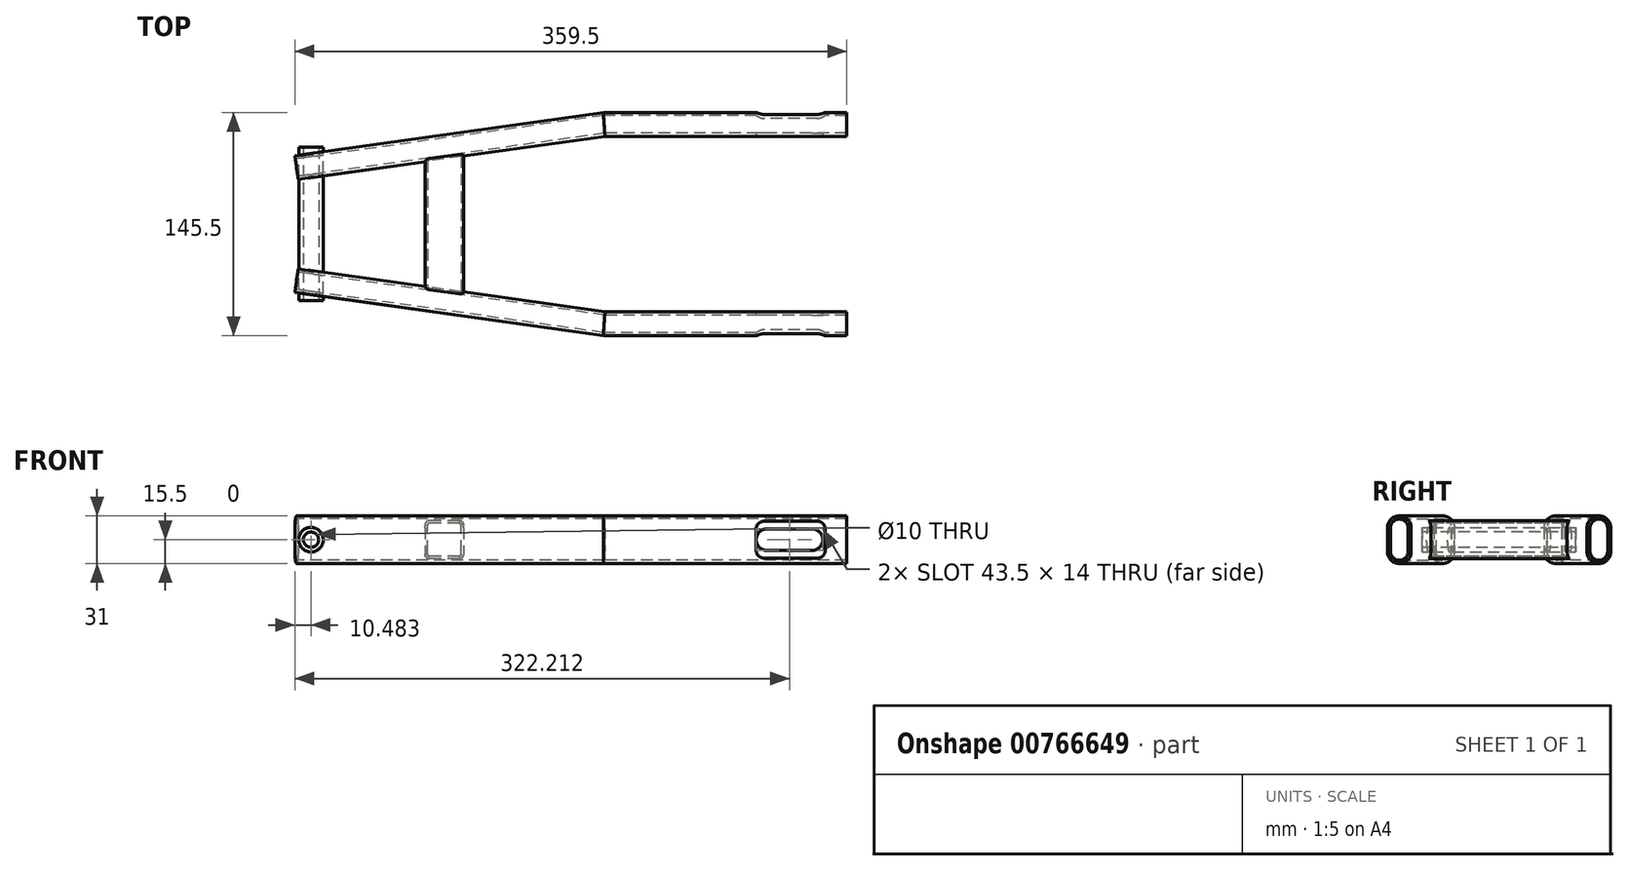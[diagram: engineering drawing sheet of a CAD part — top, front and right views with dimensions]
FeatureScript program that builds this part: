
annotation { "Feature Type Name" : "Feature", "Feature Type Description" : "" }
export const myFeature = defineFeature(function(context is Context, id is Id, definition is map)
    precondition{}
    {
        {
            var Q0;
            Q0=qCreatedBy(makeId("Top.planeOp"),FACE);
            var sketch = newSketch(context, id + "F0", { "sketchPlane" : qUnion([Q0])});
            skLineSegment(sketch, "E0", {"start": v(150.18, 0) * mm, "end": v(-148.55, 0) * mm, "construction": true});
            skLineSegment(sketch, "E1", {"start": v(150.18, 65) * mm, "end": v(-150.97, 65) * mm, "construction": true});
            skLineSegment(sketch, "E2", {"start": v(150.18, 65) * mm, "end": v(-7.85, 65) * mm});
            skLineSegment(sketch, "E3", {"start": v(-7.85, 65) * mm, "end": v(-208.24, 36.84) * mm});
            skSolve(sketch);
        }
        {
            var Q0;
            Q0=sQuery(id+"F0.wireOp",VERTEX,"E0.start");
            var Q1;
            Q1=qCreatedBy(makeId("Right.planeOp"),FACE);
            cPlane(context, id + "F1", {"entities" : qUnion([Q0, Q1]), "cplaneType" : CPlaneType.PLANE_POINT, "offset" : 25 * mm, "width" : 150 * mm, "height" : 150 * mm});
        }
        {
            var Q0;
            Q0=qCreatedBy(id+"F1.planeOp",FACE);
            var sketch = newSketch(context, id + "F2", { "sketchPlane" : qUnion([Q0])});
            skPoint(sketch, "E4.middle", {"position": v(47.26, 0) * mm});
            skLineSegment(sketch, "E5.left", {"start": v(57.25, 7.75) * mm, "end": v(57.25, -7.75) * mm});
            skLineSegment(sketch, "E5.right", {"start": v(72.75, 7.75) * mm, "end": v(72.75, -7.75) * mm});
            skPoint(sketch, "E5.middle", {"position": v(65, 0) * mm});
            skArc(sketch, "E6", {"start": v(57.25, 7.75) * mm, "mid": v(65, 15.5) * mm, "end": v(72.75, 7.75) * mm});
            skArc(sketch, "E7", {"start": v(57.25, -7.75) * mm, "mid": v(65, -15.5) * mm, "end": v(72.75, -7.75) * mm});
            skLineSegment(sketch, "E8.0", {"start": v(59.25, 7.75) * mm, "end": v(59.25, -7.75) * mm});
            skLineSegment(sketch, "E9.MirrorCS", {"start": v(70.75, 7.75) * mm, "end": v(70.75, -7.75) * mm});
            skPoint(sketch, "E10.start.orphan", {"position": v(65, 15.5) * mm});
            skPoint(sketch, "E11.trimOffspring.end.orphan", {"position": v(65, -15.5) * mm});
            skArc(sketch, "E12", {"start": v(59.25, 7.75) * mm, "mid": v(65, 13.5) * mm, "end": v(70.75, 7.75) * mm});
            skArc(sketch, "E13", {"start": v(59.25, -7.75) * mm, "mid": v(65, -13.5) * mm, "end": v(70.75, -7.75) * mm});
            skSolve(sketch);
        }
        {
            var Q0;
            Q0 = qSketchRegion(id + "F2", true);
            var Q1;
            Q1 = qConstructionFilter(qBodyType(qCreatedBy(id + "F0" ,EDGE), BodyType.WIRE), ConstructionObject.NO);
            sweep(context, id + "F3", {"profiles" : qUnion([Q0]), "path" : qUnion([Q1])});
        }
        {
            var Q0;
            Q0=makeQuery(id+"F3.opSweep","SWEPT_FACE",FACE,{"disambiguationData":[OSD([sQuery(id+"F0.wireOp",EDGE,"E2"),sQuery(id+"F2.wireOp",EDGE,"E5.left")])]});
            var sketch = newSketch(context, id + "F4", { "sketchPlane" : qUnion([Q0])});
            skLineSegment(sketch, "E14.bottom", {"start": v(127.64, -7) * mm, "end": v(98.14, -7) * mm});
            skLineSegment(sketch, "E14.top", {"start": v(127.64, 7) * mm, "end": v(98.14, 7) * mm});
            skPoint(sketch, "E14.middle", {"position": v(112.9, 0) * mm});
            skArc(sketch, "E15", {"start": v(127.64, 7) * mm, "mid": v(134.64, 0) * mm, "end": v(127.64, -7) * mm});
            skArc(sketch, "E16", {"start": v(98.14, 7) * mm, "mid": v(91.14, 0) * mm, "end": v(98.14, -7) * mm});
            skSolve(sketch);
        }
        {
            var Q0;
            Q0 = qSketchRegion(id + "F4", true);
            extrude(context, id + "F5", {"entities" : qUnion([Q0]), "operationType" : NewBodyOperationType.REMOVE, "endBound" : BoundingType.UP_TO_NEXT, "oppositeDirection" : true, "depth" : 25 * mm, "offsetDistance" : 25 * mm});
        }
        {
            var Q0;
            Q0=makeQuery(id+"F3.opSweep","SWEPT_BODY",BODY,{"disambiguationData":[OSD([sQuery(id+"F0.wireOp",EDGE,"E3"),sQuery(id+"F2.wireOp",EDGE,"E5.left"),sQuery(id+"F2.wireOp",EDGE,"E5.right"),sQuery(id+"F2.wireOp",EDGE,"E6"),sQuery(id+"F2.wireOp",EDGE,"E7"),sQuery(id+"F2.wireOp",EDGE,"E8.0"),sQuery(id+"F2.wireOp",EDGE,"E9.MirrorCS"),sQuery(id+"F2.wireOp",EDGE,"E12"),sQuery(id+"F2.wireOp",EDGE,"E13")])]});
            var Q1;
            Q1=qCreatedBy(makeId("Front.planeOp"),FACE);
            mirror(context, id + "F6", {"entities" : qUnion([Q0]), "mirrorPlane" : qUnion([Q1])});
        }
        {
            var Q0;
            Q0=makeQuery(id+"F6.opPattern","COPY",FACE,{"derivedFrom":makeQuery(id+"F3.opSweep","SWEPT_FACE",FACE,{"disambiguationData":[OSD([sQuery(id+"F0.wireOp",EDGE,"E2"),sQuery(id+"F2.wireOp",EDGE,"E5.right")])]}),"instanceName":"1"});
            var sketch = newSketch(context, id + "F7", { "sketchPlane" : qUnion([Q0])});
            skLineSegment(sketch, "E17.bottom", {"start": v(96.18, 12) * mm, "end": v(131.18, 12) * mm});
            skLineSegment(sketch, "E17.top", {"start": v(96.18, -12) * mm, "end": v(131.18, -12) * mm});
            skLineSegment(sketch, "E17.left", {"start": v(91.18, 7) * mm, "end": v(91.18, -7) * mm});
            skLineSegment(sketch, "E17.right", {"start": v(136.18, 7) * mm, "end": v(136.18, -7) * mm});
            skPoint(sketch, "E17.middle", {"position": v(113.68, 0) * mm});
            skPoint(sketch, "E18.visualSharp", {"position": v(91.18, 12) * mm});
            skArc(sketch, "E18.filletArc", {"start": v(96.18, 12) * mm, "mid": v(92.65, 10.54) * mm, "end": v(91.18, 7) * mm});
            skPoint(sketch, "E19.visualSharp", {"position": v(91.18, -12) * mm});
            skArc(sketch, "E19.filletArc", {"start": v(91.18, -7) * mm, "mid": v(92.65, -10.54) * mm, "end": v(96.18, -12) * mm});
            skPoint(sketch, "E20.visualSharp", {"position": v(136.18, 12) * mm});
            skArc(sketch, "E20.filletArc", {"start": v(136.18, 7) * mm, "mid": v(134.72, 10.54) * mm, "end": v(131.18, 12) * mm});
            skPoint(sketch, "E21.visualSharp", {"position": v(136.18, -12) * mm});
            skArc(sketch, "E21.filletArc", {"start": v(131.18, -12) * mm, "mid": v(134.72, -10.54) * mm, "end": v(136.18, -7) * mm});
            skSolve(sketch);
        }
        {
            var Q0;
            Q0 = qSketchRegion(id + "F7", true);
            extrude(context, id + "F8", {"entities" : qUnion([Q0]), "operationType" : NewBodyOperationType.REMOVE, "endBound" : BoundingType.UP_TO_NEXT, "oppositeDirection" : true, "depth" : 25 * mm, "offsetDistance" : 25 * mm});
        }
        {
            var Q0;
            Q0=makeQuery(id+"F3.opSweep","SWEPT_FACE",FACE,{"disambiguationData":[OSD([sQuery(id+"F0.wireOp",EDGE,"E2"),sQuery(id+"F2.wireOp",EDGE,"E5.right")])]});
            var sketch = newSketch(context, id + "F9", { "sketchPlane" : qUnion([Q0])});
            skLineSegment(sketch, "E22.bottom", {"start": v(-131.18, 12) * mm, "end": v(-96.18, 12) * mm});
            skLineSegment(sketch, "E22.top", {"start": v(-131.18, -12) * mm, "end": v(-96.18, -12) * mm});
            skLineSegment(sketch, "E22.left", {"start": v(-136.18, 7) * mm, "end": v(-136.18, -7) * mm});
            skLineSegment(sketch, "E22.right", {"start": v(-91.18, 7) * mm, "end": v(-91.18, -7) * mm});
            skPoint(sketch, "E22.middle", {"position": v(-113.68, 0) * mm});
            skPoint(sketch, "E23.visualSharp", {"position": v(-136.18, 12) * mm});
            skArc(sketch, "E23.filletArc", {"start": v(-131.18, 12) * mm, "mid": v(-134.72, 10.54) * mm, "end": v(-136.18, 7) * mm});
            skPoint(sketch, "E24.visualSharp", {"position": v(-136.18, -12) * mm});
            skArc(sketch, "E24.filletArc", {"start": v(-136.18, -7) * mm, "mid": v(-134.72, -10.54) * mm, "end": v(-131.18, -12) * mm});
            skPoint(sketch, "E25.visualSharp", {"position": v(-91.18, 12) * mm});
            skArc(sketch, "E25.filletArc", {"start": v(-91.18, 7) * mm, "mid": v(-92.65, 10.54) * mm, "end": v(-96.18, 12) * mm});
            skPoint(sketch, "E26.visualSharp", {"position": v(-91.18, -12) * mm});
            skArc(sketch, "E26.filletArc", {"start": v(-96.18, -12) * mm, "mid": v(-92.65, -10.54) * mm, "end": v(-91.18, -7) * mm});
            skSolve(sketch);
        }
        {
            var Q0;
            Q0 = qSketchRegion(id + "F9", true);
            extrude(context, id + "F10", {"entities" : qUnion([Q0]), "operationType" : NewBodyOperationType.REMOVE, "endBound" : BoundingType.UP_TO_NEXT, "oppositeDirection" : true, "depth" : 25 * mm, "offsetDistance" : 25 * mm});
        }
        {
            var Q0;
            Q0=qCreatedBy(makeId("Front.planeOp"),FACE);
            var sketch = newSketch(context, id + "F11", { "sketchPlane" : qUnion([Q0])});
            skCircle(sketch, "E27", {"center": v(-198.84, 0) * mm, "radius": 8 * mm});
            skSolve(sketch);
        }
        {
            var Q0;
            Q0 = qSketchRegion(id + "F11", true);
            extrude(context, id + "F12", {"entities" : qUnion([Q0]), "operationType" : NewBodyOperationType.ADD, "endBound" : BoundingType.SYMMETRIC, "depth" : 100 * mm, "offsetDistance" : 25 * mm});
        }
        {
            var Q0;
            Q0=makeQuery(id+"F12.opExtrude","CAP_FACE",FACE,{"disambiguationData":[OSD([sQuery(id+"F11.wireOp",EDGE,"E27")])],"isStart":false});
            var sketch = newSketch(context, id + "F13", { "sketchPlane" : qUnion([Q0])});
            skCircle(sketch, "E28", {"center": v(-198.84, 0) * mm, "radius": 5 * mm});
            skSolve(sketch);
        }
        {
            var Q0;
            Q0 = qSketchRegion(id + "F13", true);
            extrude(context, id + "F14", {"entities" : qUnion([Q0]), "operationType" : NewBodyOperationType.REMOVE, "oppositeDirection" : true, "depth" : 100 * mm, "offsetDistance" : 25 * mm});
        }
        {
            var Q0;
            Q0=qCreatedBy(makeId("Front.planeOp"),FACE);
            var sketch = newSketch(context, id + "F15", { "sketchPlane" : qUnion([Q0])});
            skLineSegment(sketch, "E29.bottom", {"start": v(-102.5, -12.5) * mm, "end": v(-121.5, -12.5) * mm});
            skLineSegment(sketch, "E29.top", {"start": v(-102.5, 12.5) * mm, "end": v(-121.5, 12.5) * mm});
            skLineSegment(sketch, "E29.left", {"start": v(-99.5, -9.5) * mm, "end": v(-99.5, 9.5) * mm});
            skLineSegment(sketch, "E29.right", {"start": v(-124.5, -9.5) * mm, "end": v(-124.5, 9.5) * mm});
            skPoint(sketch, "E29.middle", {"position": v(-112, 0) * mm});
            skLineSegment(sketch, "E30.bottom", {"start": v(-121.5, -10.9) * mm, "end": v(-102.5, -10.9) * mm});
            skLineSegment(sketch, "E30.top", {"start": v(-121.5, 10.9) * mm, "end": v(-102.5, 10.9) * mm});
            skLineSegment(sketch, "E30.left", {"start": v(-122.9, -9.5) * mm, "end": v(-122.9, 9.5) * mm});
            skLineSegment(sketch, "E30.right", {"start": v(-101.1, -9.5) * mm, "end": v(-101.1, 9.5) * mm});
            skPoint(sketch, "E31.visualSharp", {"position": v(-122.9, 10.9) * mm});
            skArc(sketch, "E31.filletArc", {"start": v(-121.5, 10.9) * mm, "mid": v(-122.5, 10.49) * mm, "end": v(-122.9, 9.5) * mm});
            skPoint(sketch, "E32.visualSharp", {"position": v(-101.1, 10.9) * mm});
            skArc(sketch, "E32.filletArc", {"start": v(-101.1, 9.5) * mm, "mid": v(-101.52, 10.49) * mm, "end": v(-102.5, 10.9) * mm});
            skPoint(sketch, "E33.visualSharp", {"position": v(-101.1, -10.9) * mm});
            skArc(sketch, "E33.filletArc", {"start": v(-102.5, -10.9) * mm, "mid": v(-101.52, -10.49) * mm, "end": v(-101.1, -9.5) * mm});
            skPoint(sketch, "E34.visualSharp", {"position": v(-122.9, -10.9) * mm});
            skArc(sketch, "E34.filletArc", {"start": v(-122.9, -9.5) * mm, "mid": v(-122.5, -10.49) * mm, "end": v(-121.5, -10.9) * mm});
            skPoint(sketch, "E35.visualSharp", {"position": v(-124.5, -12.5) * mm});
            skArc(sketch, "E35.filletArc", {"start": v(-124.5, -9.5) * mm, "mid": v(-123.63, -11.62) * mm, "end": v(-121.5, -12.5) * mm});
            skPoint(sketch, "E36.visualSharp", {"position": v(-99.5, -12.5) * mm});
            skArc(sketch, "E36.filletArc", {"start": v(-102.5, -12.5) * mm, "mid": v(-100.39, -11.62) * mm, "end": v(-99.5, -9.5) * mm});
            skPoint(sketch, "E37.visualSharp", {"position": v(-99.5, 12.5) * mm});
            skArc(sketch, "E37.filletArc", {"start": v(-99.5, 9.5) * mm, "mid": v(-100.39, 11.62) * mm, "end": v(-102.5, 12.5) * mm});
            skPoint(sketch, "E38.visualSharp", {"position": v(-124.5, 12.5) * mm});
            skArc(sketch, "E38.filletArc", {"start": v(-121.5, 12.5) * mm, "mid": v(-123.63, 11.62) * mm, "end": v(-124.5, 9.5) * mm});
            skSolve(sketch);
        }
        {
            var Q0;
            Q0 = qSketchRegion(id + "F15", true);
            var Q1;
            {var subQ1=sQuery(id+"F0.wireOp",EDGE,"E2");var subQ3=sQuery(id+"F0.wireOp",EDGE,"E3");var subQ4=sQuery(id+"F2.wireOp",EDGE,"E5.left");Q1=makeQuery(id+"F12.boolean.opBoolean","SPLIT",FACE,{"disambiguationData":[TD([makeQuery(id+"F3.opSweep","SWEPT_FACE",FACE,{"disambiguationData":[OSD([subQ1,subQ4])]})])],"derivedFrom":makeQuery(id+"F3.opSweep","SWEPT_FACE",FACE,{"disambiguationData":[OSD([subQ3,subQ4])]})});}
            var Q2;
            Q2=makeQuery(id+"F3.opSweep","SWEPT_BODY",BODY,{"disambiguationData":[OSD([sQuery(id+"F0.wireOp",EDGE,"E3"),sQuery(id+"F2.wireOp",EDGE,"E5.left"),sQuery(id+"F2.wireOp",EDGE,"E5.right"),sQuery(id+"F2.wireOp",EDGE,"E6"),sQuery(id+"F2.wireOp",EDGE,"E7"),sQuery(id+"F2.wireOp",EDGE,"E8.0"),sQuery(id+"F2.wireOp",EDGE,"E9.MirrorCS"),sQuery(id+"F2.wireOp",EDGE,"E12"),sQuery(id+"F2.wireOp",EDGE,"E13")])]});
            var Q3;
            {var subQ1=sQuery(id+"F0.wireOp",EDGE,"E3");var subQ2=sQuery(id+"F2.wireOp",EDGE,"E6");var subQ3=sQuery(id+"F0.wireOp",EDGE,"E2");var subQ4=sQuery(id+"F2.wireOp",EDGE,"E5.left");Q3=makeQuery(id+"F12.boolean.opBoolean","SPLIT",FACE,{"disambiguationData":[TD([makeQuery(id+"F6.opPattern","COPY",FACE,{"derivedFrom":makeQuery(id+"F3.opSweep","SWEPT_FACE",FACE,{"disambiguationData":[OSD([subQ3,subQ2])]}),"instanceName":"1"})])],"derivedFrom":makeQuery(id+"F6.opPattern","COPY",FACE,{"derivedFrom":makeQuery(id+"F3.opSweep","SWEPT_FACE",FACE,{"disambiguationData":[OSD([subQ1,subQ4])]}),"instanceName":"1"})});}
            var Q4;
            Q4=makeQuery(id+"F3.opSweep","SWEPT_BODY",BODY,{"disambiguationData":[OSD([sQuery(id+"F0.wireOp",EDGE,"E3"),sQuery(id+"F2.wireOp",EDGE,"E5.left"),sQuery(id+"F2.wireOp",EDGE,"E5.right"),sQuery(id+"F2.wireOp",EDGE,"E6"),sQuery(id+"F2.wireOp",EDGE,"E7"),sQuery(id+"F2.wireOp",EDGE,"E8.0"),sQuery(id+"F2.wireOp",EDGE,"E9.MirrorCS"),sQuery(id+"F2.wireOp",EDGE,"E12"),sQuery(id+"F2.wireOp",EDGE,"E13")])]});
            extrude(context, id + "F16", {"entities" : qUnion([Q0]), "operationType" : NewBodyOperationType.ADD, "endBound" : BoundingType.UP_TO_BODY, "oppositeDirection" : true, "depth" : 25 * mm, "endBoundEntityFace" : qUnion([Q1]), "endBoundEntityBody" : qUnion([Q2]), "offsetDistance" : 25 * mm, "hasSecondDirection" : true, "secondDirectionBound" : SecondDirectionBoundingType.UP_TO_BODY, "secondDirectionOppositeDirection" : false, "secondDirectionDepth" : 25 * mm, "secondDirectionBoundEntityFace" : qUnion([Q3]), "secondDirectionBoundEntityBody" : qUnion([Q4])});
        }
    });
